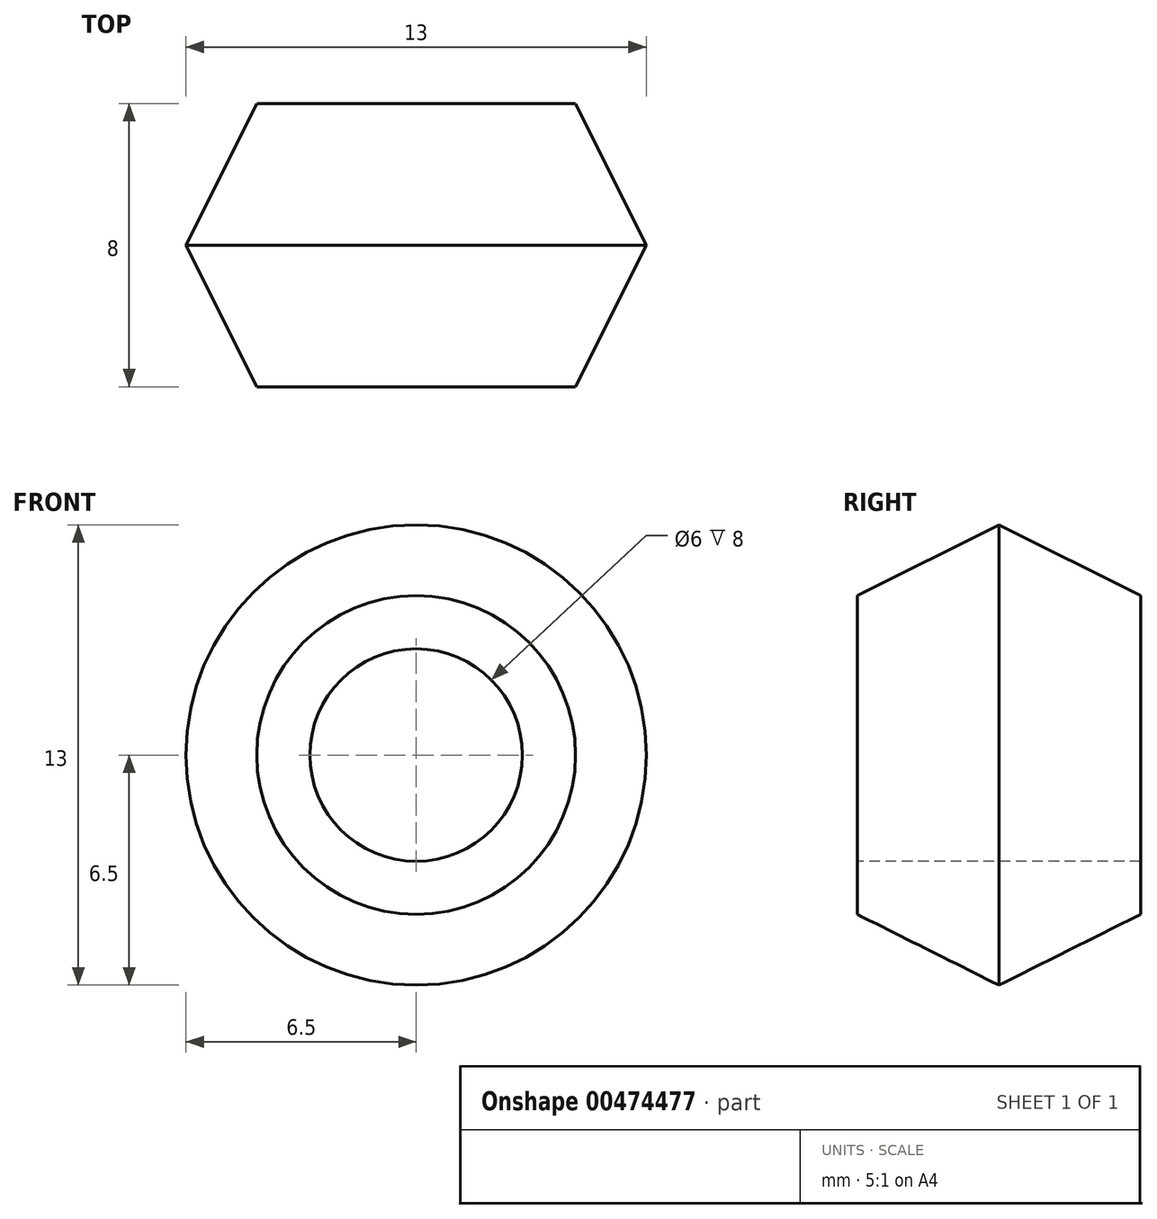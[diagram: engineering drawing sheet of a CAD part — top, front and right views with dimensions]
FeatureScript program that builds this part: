
annotation { "Feature Type Name" : "Feature", "Feature Type Description" : "" }
export const myFeature = defineFeature(function(context is Context, id is Id, definition is map)
    precondition{}
    {
        {
            var Q0;
            Q0=qCreatedBy(makeId("Right.planeOp"),FACE);
            var sketch = newSketch(context, id + "F0", { "sketchPlane" : qUnion([Q0])});
            skLineSegment(sketch, "E0", {"start": v(0, 0) * mm, "end": v(4, 0) * mm});
            skLineSegment(sketch, "E1", {"start": v(4, 3) * mm, "end": v(4, 4.5) * mm});
            skLineSegment(sketch, "E2", {"start": v(4, 4.5) * mm, "end": v(0, 6.5) * mm});
            skLineSegment(sketch, "E3", {"start": v(0, 6.5) * mm, "end": v(-4, 4.5) * mm});
            skLineSegment(sketch, "E4", {"start": v(-4, 4.5) * mm, "end": v(-4, 3) * mm});
            skLineSegment(sketch, "E5", {"start": v(-4, 0) * mm, "end": v(0, 0) * mm});
            skLineSegment(sketch, "E6", {"start": v(-4, 3) * mm, "end": v(4, 3) * mm});
            skSolve(sketch);
        }
        {
            var Q0;
            Q0 = qSketchRegion(id + "F0", true);
            var Q1;
            Q1=sQuery(id+"F0.wireOp",EDGE,"E5");
            revolve(context, id + "F1", {"entities" : qUnion([Q0]), "axis" : qUnion([Q1]), "revolveType" : RevolveType.FULL});
        }
    });
